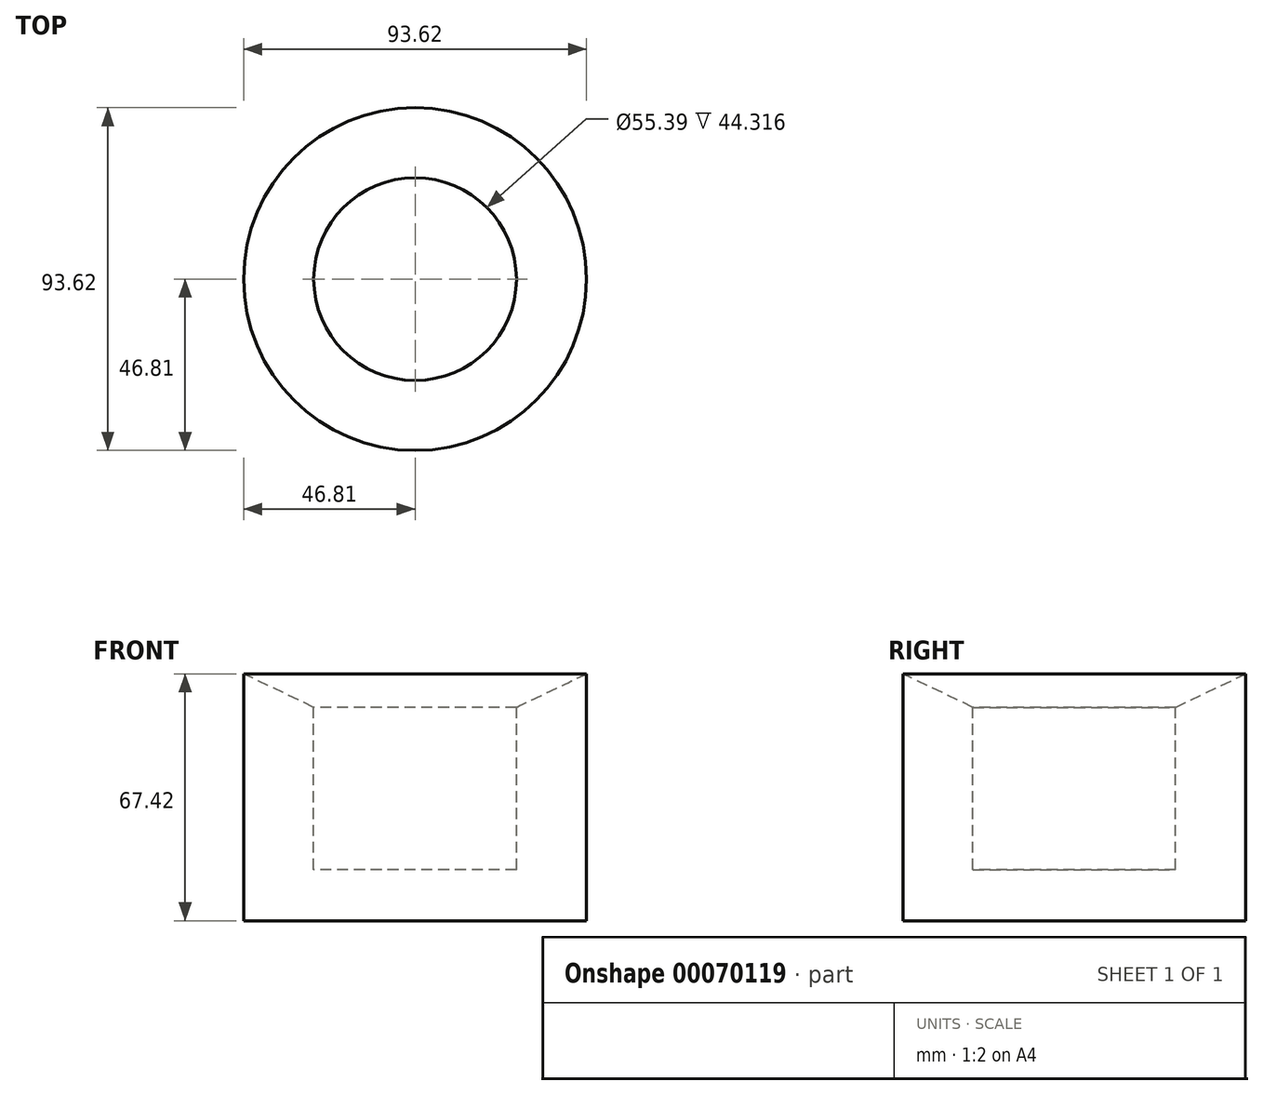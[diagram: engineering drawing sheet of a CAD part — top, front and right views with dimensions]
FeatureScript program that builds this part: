
annotation { "Feature Type Name" : "Feature", "Feature Type Description" : "" }
export const myFeature = defineFeature(function(context is Context, id is Id, definition is map)
    precondition{}
    {
        {
            var Q0;
            Q0=qCreatedBy(makeId("Front.planeOp"),FACE);
            var sketch = newSketch(context, id + "F0", { "sketchPlane" : qUnion([Q0])});
            skLineSegment(sketch, "E0", {"start": v(0, 0) * mm, "end": v(-46.81, 0) * mm});
            skLineSegment(sketch, "E1", {"start": v(-46.81, 0) * mm, "end": v(-46.81, 67.42) * mm});
            skLineSegment(sketch, "E2", {"start": v(-46.81, 67.42) * mm, "end": v(-27.7, 58.3) * mm});
            skLineSegment(sketch, "E3", {"start": v(-27.7, 58.3) * mm, "end": v(-27.7, 13.98) * mm});
            skLineSegment(sketch, "E4", {"start": v(-27.7, 13.98) * mm, "end": v(0, 13.98) * mm});
            skLineSegment(sketch, "E5", {"start": v(0, 13.98) * mm, "end": v(0, 0) * mm});
            skSolve(sketch);
        }
        {
            var Q0;
            Q0=makeQuery(id+"F0.imprint","IMPRINT",FACE,{"disambiguationData":[TD([[makeQuery(id+"F0.imprint","IMPRINT",EDGE,{"derivedFrom":sQuery(id+"F0.wireOp",EDGE,"E0")}),-1.0]])]});
            var Q1;
            Q1=sQuery(id+"F0.wireOp",EDGE,"E5");
            revolve(context, id + "F1", {"entities" : qUnion([Q0]), "axis" : qUnion([Q1]), "revolveType" : RevolveType.FULL});
        }
    });
